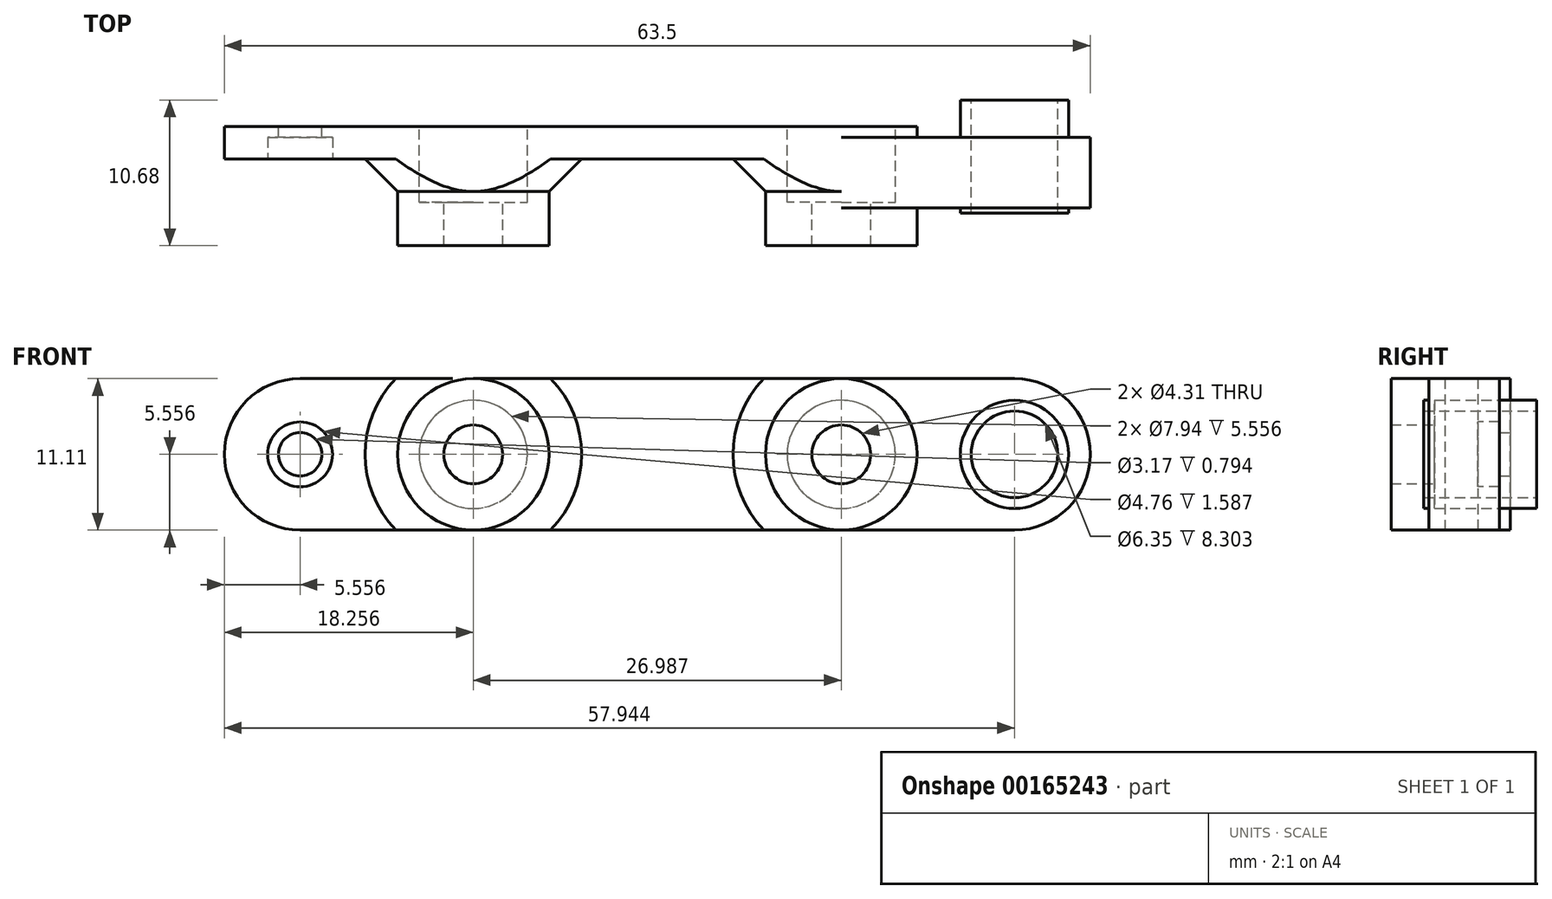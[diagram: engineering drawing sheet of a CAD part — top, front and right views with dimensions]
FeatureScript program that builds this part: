
annotation { "Feature Type Name" : "Feature", "Feature Type Description" : "" }
export const myFeature = defineFeature(function(context is Context, id is Id, definition is map)
    precondition{}
    {
        {
            var Q0;
            Q0=qCreatedBy(makeId("Top.planeOp"),FACE);
            var sketch = newSketch(context, id + "F0", { "sketchPlane" : qUnion([Q0])});
            skLineSegment(sketch, "E0.bottom", {"start": v(0, 0) * mm, "end": v(-12.7, 0) * mm});
            skLineSegment(sketch, "E0.top", {"start": v(38.1, 2.38) * mm, "end": v(-12.7, 2.38) * mm});
            skLineSegment(sketch, "E0.right", {"start": v(-12.7, 0) * mm, "end": v(-12.7, 2.38) * mm});
            skLineSegment(sketch, "E1.left", {"start": v(0, 0) * mm, "end": v(0, -6.35) * mm});
            skLineSegment(sketch, "E1.right", {"start": v(38.1, -3.57) * mm, "end": v(38.1, -6.35) * mm});
            skLineSegment(sketch, "E2", {"start": v(38.1, -3.57) * mm, "end": v(50.8, -3.57) * mm});
            skLineSegment(sketch, "E3", {"start": v(50.8, -3.57) * mm, "end": v(50.8, 1.59) * mm});
            skLineSegment(sketch, "E4", {"start": v(0, -6.35) * mm, "end": v(11.11, -6.35) * mm});
            skLineSegment(sketch, "E5", {"start": v(11.11, -6.35) * mm, "end": v(11.11, 0) * mm});
            skLineSegment(sketch, "E6", {"start": v(11.11, 0) * mm, "end": v(26.99, 0) * mm});
            skLineSegment(sketch, "E7", {"start": v(26.99, 0) * mm, "end": v(26.99, -6.35) * mm});
            skLineSegment(sketch, "E8", {"start": v(26.99, -6.35) * mm, "end": v(38.1, -6.35) * mm});
            skLineSegment(sketch, "E9", {"start": v(38.1, 2.38) * mm, "end": v(38.1, 1.59) * mm});
            skLineSegment(sketch, "E10", {"start": v(38.1, 1.59) * mm, "end": v(50.8, 1.59) * mm});
            skLineSegment(sketch, "E11", {"start": v(38.1, -6.35) * mm, "end": v(38.1, -8.73) * mm, "construction": true});
            skLineSegment(sketch, "E12", {"start": v(38.1, -8.73) * mm, "end": v(50.8, -8.73) * mm, "construction": true});
            skLineSegment(sketch, "E13", {"start": v(50.8, -8.73) * mm, "end": v(50.8, -3.57) * mm, "construction": true});
            skSolve(sketch);
        }
        {
            var Q0;
            Q0 = qSketchRegion(id + "F0", true);
            extrude(context, id + "F1", {"entities" : qUnion([Q0]), "depth" : 11.1 * mm});
        }
        {
            var Q0;
            Q0=makeQuery(id+"F1.opExtrude","SWEPT_FACE",FACE,{"disambiguationData":[OSD([sQuery(id+"F0.wireOp",EDGE,"E0.top")])]});
            var sketch = newSketch(context, id + "F2", { "sketchPlane" : qUnion([Q0])});
            skCircle(sketch, "E14", {"center": v(-45.24, 5.56) * mm, "radius": 3.18 * mm});
            skCircle(sketch, "E15", {"center": v(7.14, 5.56) * mm, "radius": 1.59 * mm});
            skLineSegment(sketch, "E16", {"start": v(-32.54, 0) * mm, "end": v(-32.54, 11.11) * mm, "construction": true});
            skLineSegment(sketch, "E17", {"start": v(-5.56, 0) * mm, "end": v(-5.56, 11.11) * mm, "construction": true});
            skCircle(sketch, "E18", {"center": v(-5.56, 5.56) * mm, "radius": 2.15 * mm});
            skCircle(sketch, "E19", {"center": v(-32.54, 5.56) * mm, "radius": 2.15 * mm});
            skLineSegment(sketch, "E20", {"start": v(12.7, 5.56) * mm, "end": v(7.14, 5.56) * mm, "construction": true});
            skLineSegment(sketch, "E21", {"start": v(7.14, 5.56) * mm, "end": v(7.14, 11.11) * mm, "construction": true});
            skLineSegment(sketch, "E22", {"start": v(-45.24, 5.56) * mm, "end": v(-45.24, 11.11) * mm, "construction": true});
            skLineSegment(sketch, "E23", {"start": v(-45.24, 5.56) * mm, "end": v(-50.8, 5.56) * mm, "construction": true});
            skSolve(sketch);
        }
        {
            var Q0;
            Q0 = qSketchRegion(id + "F2", true);
            var Q1;
            Q1=makeQuery(id+"F1.opExtrude","SWEPT_FACE",FACE,{"disambiguationData":[OSD([sQuery(id+"F0.wireOp",EDGE,"E8")])]});
            extrude(context, id + "F3", {"entities" : qUnion([Q0]), "operationType" : NewBodyOperationType.REMOVE, "endBound" : BoundingType.UP_TO_SURFACE, "oppositeDirection" : true, "endBoundEntityFace" : qUnion([Q1]), "depth" : 25.4 * mm});
        }
        {
            var Q0;
            Q0=makeQuery(id+"F1.opExtrude","SWEPT_FACE",FACE,{"disambiguationData":[OSD([sQuery(id+"F0.wireOp",EDGE,"E0.bottom")])]});
            var sketch = newSketch(context, id + "F4", { "sketchPlane" : qUnion([Q0])});
            skCircle(sketch, "E24", {"center": v(-7.14, 5.56) * mm, "radius": 2.38 * mm});
            skSolve(sketch);
        }
        {
            var Q0;
            Q0 = qSketchRegion(id + "F4", true);
            extrude(context, id + "F5", {"entities" : qUnion([Q0]), "operationType" : NewBodyOperationType.REMOVE, "oppositeDirection" : true, "depth" : 1.59 * mm});
        }
        {
            var Q0;
            Q0=makeQuery(id+"F1.opExtrude","SWEPT_FACE",FACE,{"disambiguationData":[OSD([sQuery(id+"F0.wireOp",EDGE,"E10")])]});
            var sketch = newSketch(context, id + "F6", { "sketchPlane" : qUnion([Q0])});
            skCircle(sketch, "E25", {"center": v(-45.24, 5.56) * mm, "radius": 3.18 * mm});
            skCircle(sketch, "E26", {"center": v(-45.24, 5.56) * mm, "radius": 3.97 * mm});
            skSolve(sketch);
        }
        {
            var Q0;
            Q0 = qSketchRegion(id + "F6", true);
            var Q1;
            Q1=makeQuery(id+"F1.opExtrude","SWEPT_FACE",FACE,{"disambiguationData":[OSD([sQuery(id+"F0.wireOp",EDGE,"E0.top")])]});
            extrude(context, id + "F7", {"entities" : qUnion([Q0]), "operationType" : NewBodyOperationType.ADD, "endBoundEntityFace" : qUnion([Q1]), "depth" : 2.75 * mm, "hasSecondDirection" : true, "secondDirectionOppositeDirection" : true, "secondDirectionDepth" : 5.56 * mm});
        }
        {
            var Q0;
            Q0=makeQuery(id+"F1.opExtrude","CAP_EDGE",EDGE,{"disambiguationData":[OSD([sQuery(id+"F0.wireOp",EDGE,"E1.left")])],"isStart":true});
            var Q1;
            Q1=makeQuery(id+"F1.opExtrude","CAP_EDGE",EDGE,{"disambiguationData":[OSD([sQuery(id+"F0.wireOp",EDGE,"E1.left")])],"isStart":false});
            var Q2;
            Q2=makeQuery(id+"F1.opExtrude","CAP_EDGE",EDGE,{"disambiguationData":[OSD([sQuery(id+"F0.wireOp",EDGE,"E1.right")])],"isStart":true});
            var Q3;
            Q3=makeQuery(id+"F1.opExtrude","CAP_EDGE",EDGE,{"disambiguationData":[OSD([sQuery(id+"F0.wireOp",EDGE,"E1.right")])],"isStart":false});
            var Q4;
            Q4=makeQuery(id+"F1.opExtrude","CAP_EDGE",EDGE,{"disambiguationData":[OSD([sQuery(id+"F0.wireOp",EDGE,"E9")])],"isStart":true});
            var Q5;
            Q5=makeQuery(id+"F1.opExtrude","CAP_EDGE",EDGE,{"disambiguationData":[OSD([sQuery(id+"F0.wireOp",EDGE,"E9")])],"isStart":false});
            var Q6;
            Q6=makeQuery(id+"F1.opExtrude","CAP_EDGE",EDGE,{"disambiguationData":[OSD([sQuery(id+"F0.wireOp",EDGE,"E5")])],"isStart":false});
            var Q7;
            Q7=makeQuery(id+"F1.opExtrude","CAP_EDGE",EDGE,{"disambiguationData":[OSD([sQuery(id+"F0.wireOp",EDGE,"E5")])],"isStart":true});
            var Q8;
            Q8=makeQuery(id+"F1.opExtrude","CAP_EDGE",EDGE,{"disambiguationData":[OSD([sQuery(id+"F0.wireOp",EDGE,"E7")])],"isStart":false});
            var Q9;
            Q9=makeQuery(id+"F1.opExtrude","CAP_EDGE",EDGE,{"disambiguationData":[OSD([sQuery(id+"F0.wireOp",EDGE,"E7")])],"isStart":true});
            var Q10;
            Q10=makeQuery(id+"F1.opExtrude","CAP_EDGE",EDGE,{"disambiguationData":[OSD([sQuery(id+"F0.wireOp",EDGE,"E3")])],"isStart":false});
            var Q11;
            Q11=makeQuery(id+"F1.opExtrude","CAP_EDGE",EDGE,{"disambiguationData":[OSD([sQuery(id+"F0.wireOp",EDGE,"E3")])],"isStart":true});
            var Q12;
            Q12=makeQuery(id+"F1.opExtrude","CAP_EDGE",EDGE,{"disambiguationData":[OSD([sQuery(id+"F0.wireOp",EDGE,"E0.right")])],"isStart":false});
            var Q13;
            Q13=makeQuery(id+"F1.opExtrude","CAP_EDGE",EDGE,{"disambiguationData":[OSD([sQuery(id+"F0.wireOp",EDGE,"E0.right")])],"isStart":true});
            fillet(context, id + "F8", {"entities" : qUnion([Q0, Q1, Q2, Q3, Q4, Q5, Q6, Q7, Q8, Q9, Q10, Q11, Q12, Q13]), "radius" : 5.56 * mm, "tangentPropagation" : true, "allowEdgeOverflow" : false});
        }
        {
            var Q0;
            Q0=makeQuery(id+"F1.opExtrude","SWEPT_FACE",FACE,{"disambiguationData":[OSD([sQuery(id+"F0.wireOp",EDGE,"E4")])]});
            cPlane(context, id + "F9", {"entities" : qUnion([Q0]), "cplaneType" : CPlaneType.OFFSET, "offset" : 3.17 * mm, "oppositeDirection" : true, "width" : 152.4 * mm, "height" : 152.4 * mm});
        }
        {
            var Q0;
            Q0=makeQuery(id+"F1.opExtrude","SWEPT_FACE",FACE,{"disambiguationData":[OSD([sQuery(id+"F0.wireOp",EDGE,"E0.top")])]});
            var sketch = newSketch(context, id + "F10", { "sketchPlane" : qUnion([Q0])});
            skCircle(sketch, "E27", {"center": v(-32.54, 5.56) * mm, "radius": 3.97 * mm});
            skCircle(sketch, "E28", {"center": v(-5.56, 5.56) * mm, "radius": 3.97 * mm});
            skSolve(sketch);
        }
        {
            var Q0;
            Q0 = qSketchRegion(id + "F10", true);
            var Q1;
            Q1=qCreatedBy(id+"F9.planeOp",FACE);
            extrude(context, id + "F11", {"entities" : qUnion([Q0]), "operationType" : NewBodyOperationType.REMOVE, "endBound" : BoundingType.UP_TO_SURFACE, "oppositeDirection" : true, "endBoundEntityFace" : qUnion([Q1]), "depth" : 25.4 * mm});
        }
        {
            var Q0;
            Q0=makeQuery(id+"F8.opFillet","BLEND_EDGE",EDGE,{"blendedFrom":[makeQuery(id+"F1.opExtrude","CAP_EDGE",EDGE,{"disambiguationData":[OSD([sQuery(id+"F0.wireOp",EDGE,"E5")])],"isStart":true}),makeQuery(id+"F1.opExtrude","SWEPT_FACE",FACE,{"disambiguationData":[OSD([sQuery(id+"F0.wireOp",EDGE,"E6")])]})],"blendedInto":[makeQuery(id+"F1.opExtrude","SWEPT_FACE",FACE,{"disambiguationData":[OSD([sQuery(id+"F0.wireOp",EDGE,"E6")])]})]});
            var Q1;
            Q1=makeQuery(id+"F8.opFillet","BLEND_EDGE",EDGE,{"blendedFrom":[makeQuery(id+"F1.opExtrude","CAP_EDGE",EDGE,{"disambiguationData":[OSD([sQuery(id+"F0.wireOp",EDGE,"E7")])],"isStart":true}),makeQuery(id+"F1.opExtrude","SWEPT_FACE",FACE,{"disambiguationData":[OSD([sQuery(id+"F0.wireOp",EDGE,"E6")])]})],"blendedInto":[makeQuery(id+"F1.opExtrude","SWEPT_FACE",FACE,{"disambiguationData":[OSD([sQuery(id+"F0.wireOp",EDGE,"E6")])]})]});
            chamfer(context, id + "F12", {"entities" : qUnion([Q0, Q1]), "width" : 2.38 * mm, "tangentPropagation" : true});
        }
    });
